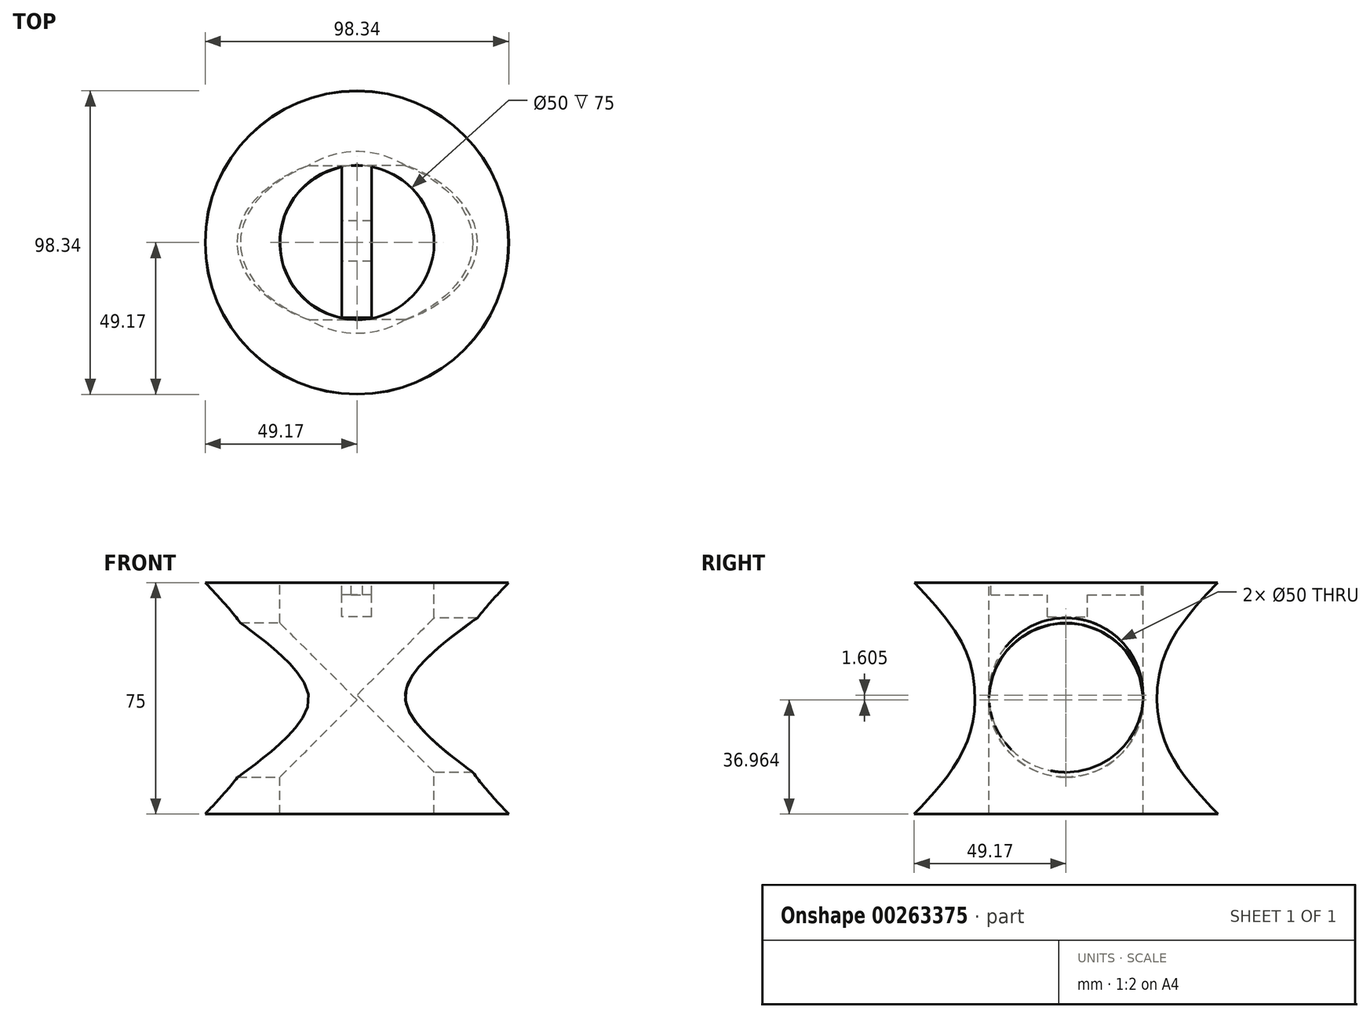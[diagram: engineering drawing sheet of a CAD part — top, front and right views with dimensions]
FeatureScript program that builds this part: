
annotation { "Feature Type Name" : "Feature", "Feature Type Description" : "" }
export const myFeature = defineFeature(function(context is Context, id is Id, definition is map)
    precondition{}
    {
        {
            var Q0;
            Q0=qCreatedBy(makeId("Top.planeOp"),FACE);
            var sketch = newSketch(context, id + "F0", { "sketchPlane" : qUnion([Q0])});
            skCircle(sketch, "E0", {"center": v(0, 0) * mm, "radius": 49.17 * mm});
            skSolve(sketch);
        }
        {
            var Q0;
            Q0=makeQuery(id+"F0.imprint","IMPRINT",FACE,{"disambiguationData":[TD([[makeQuery(id+"F0.imprint","IMPRINT",EDGE,{"derivedFrom":sQuery(id+"F0.wireOp",EDGE,"E0")}),1.0]])]});
            cPlane(context, id + "F1", {"entities" : qUnion([Q0]), "cplaneType" : CPlaneType.OFFSET, "offset" : 25 * mm, "width" : 150 * mm, "height" : 150 * mm});
        }
        {
            var Q0;
            Q0=qCreatedBy(id+"F1.planeOp",FACE);
            var sketch = newSketch(context, id + "F2", { "sketchPlane" : qUnion([Q0])});
            skCircle(sketch, "E1", {"center": v(0, 0) * mm, "radius": 31.5 * mm});
            skSolve(sketch);
        }
        {
            var Q0;
            Q0=qCreatedBy(id+"F1.planeOp",FACE);
            cPlane(context, id + "F3", {"entities" : qUnion([Q0]), "cplaneType" : CPlaneType.OFFSET, "offset" : 25 * mm, "width" : 150 * mm, "height" : 150 * mm});
        }
        {
            var Q0;
            Q0=qCreatedBy(id+"F3.planeOp",FACE);
            var sketch = newSketch(context, id + "F4", { "sketchPlane" : qUnion([Q0])});
            skCircle(sketch, "E2", {"center": v(0, 0) * mm, "radius": 31.39 * mm});
            skSolve(sketch);
        }
        {
            var Q0;
            Q0=qCreatedBy(id+"F3.planeOp",FACE);
            cPlane(context, id + "F5", {"entities" : qUnion([Q0]), "cplaneType" : CPlaneType.OFFSET, "offset" : 25 * mm, "width" : 150 * mm, "height" : 150 * mm});
        }
        {
            var Q0;
            Q0=qCreatedBy(id+"F5.planeOp",FACE);
            var sketch = newSketch(context, id + "F6", { "sketchPlane" : qUnion([Q0])});
            skCircle(sketch, "E3", {"center": v(0, 0) * mm, "radius": 49.12 * mm});
            skSolve(sketch);
        }
        {
            var Q0;
            Q0=makeQuery(id+"F0.imprint","IMPRINT",FACE,{"disambiguationData":[TD([[makeQuery(id+"F0.imprint","IMPRINT",EDGE,{"derivedFrom":sQuery(id+"F0.wireOp",EDGE,"E0")}),1.0]])]});
            var Q1;
            Q1=makeQuery(id+"F2.imprint","IMPRINT",FACE,{"disambiguationData":[TD([[makeQuery(id+"F2.imprint","IMPRINT",EDGE,{"derivedFrom":sQuery(id+"F2.wireOp",EDGE,"E1")}),1.0]])]});
            var Q2;
            Q2=makeQuery(id+"F4.imprint","IMPRINT",FACE,{"disambiguationData":[TD([[makeQuery(id+"F4.imprint","IMPRINT",EDGE,{"derivedFrom":sQuery(id+"F4.wireOp",EDGE,"E2")}),1.0]])]});
            var Q3;
            Q3=makeQuery(id+"F6.imprint","IMPRINT",FACE,{"disambiguationData":[TD([[makeQuery(id+"F6.imprint","IMPRINT",EDGE,{"derivedFrom":sQuery(id+"F6.wireOp",EDGE,"E3")}),1.0]])]});
            loft(context, id + "F7", {"sheetProfilesArray" : [{ "sheetProfileEntities" : qUnion([Q0]) }, { "sheetProfileEntities" : qUnion([Q1]) }, { "sheetProfileEntities" : qUnion([Q2]) }, { "sheetProfileEntities" : qUnion([Q3]) }]});
        }
        {
            var Q0;
            Q0=qCreatedBy(id+"F5.planeOp",FACE);
            var sketch = newSketch(context, id + "F8", { "sketchPlane" : qUnion([Q0])});
            skCircle(sketch, "E4", {"center": v(0, 0) * mm, "radius": 19.4 * mm});
            skSolve(sketch);
        }
        {
            var Q0;
            Q0=qCreatedBy(id+"F1.planeOp",FACE);
            var sketch = newSketch(context, id + "F9", { "sketchPlane" : qUnion([Q0])});
            skCircle(sketch, "E5", {"center": v(0, 0) * mm, "radius": 19.31 * mm});
            skSolve(sketch);
        }
        {
            var Q0;
            Q0=sQuery(id+"F8.wireOp",VERTEX,"E4.center");
            var Q1;
            Q1=sQuery(id+"F9.wireOp",VERTEX,"E5.center");
            var Q2;
            Q2=makeQuery(id+"F7.opLoft","SWEPT_BODY",BODY,{"disambiguationData":[OSD([makeQuery(id+"F0.imprint","IMPRINT",FACE,{"disambiguationData":[TD([[makeQuery(id+"F0.imprint","IMPRINT",EDGE,{"derivedFrom":sQuery(id+"F0.wireOp",EDGE,"E0")}),1.0]])]}),sQuery(id+"F2.wireOp",EDGE,"E1"),sQuery(id+"F4.wireOp",EDGE,"E2"),makeQuery(id+"F6.imprint","IMPRINT",FACE,{"disambiguationData":[TD([[makeQuery(id+"F6.imprint","IMPRINT",EDGE,{"derivedFrom":sQuery(id+"F6.wireOp",EDGE,"E3")}),1.0]])]})])]});
            hole(context, id + "F10", {"style" : HoleStyle.SIMPLE, "endStyle" : HoleEndStyle.BLIND, "holeDiameter" : 50 * mm, "holeDepth" : 75 * mm, "tappedDepth" : 12 * mm, "tapClearance" : 3, "startFromSketch" : true, "locations" : qUnion([Q0, Q1]), "scope" : qUnion([Q2])});
        }
        {
            var Q0;
            Q0=qCreatedBy(makeId("Right.planeOp"),FACE);
            var sketch = newSketch(context, id + "F11", { "sketchPlane" : qUnion([Q0])});
            skCircle(sketch, "E6", {"center": v(0, 38.57) * mm, "radius": 15 * mm});
            skSolve(sketch);
        }
        {
            var Q0;
            Q0=sQuery(id+"F11.wireOp",VERTEX,"E6.center");
            var Q1;
            Q1=makeQuery(id+"F7.opLoft","SWEPT_BODY",BODY,{"disambiguationData":[OSD([makeQuery(id+"F0.imprint","IMPRINT",FACE,{"disambiguationData":[TD([[makeQuery(id+"F0.imprint","IMPRINT",EDGE,{"derivedFrom":sQuery(id+"F0.wireOp",EDGE,"E0")}),1.0]])]}),sQuery(id+"F2.wireOp",EDGE,"E1"),sQuery(id+"F4.wireOp",EDGE,"E2"),makeQuery(id+"F6.imprint","IMPRINT",FACE,{"disambiguationData":[TD([[makeQuery(id+"F6.imprint","IMPRINT",EDGE,{"derivedFrom":sQuery(id+"F6.wireOp",EDGE,"E3")}),1.0]])]})])]});
            hole(context, id + "F12", {"style" : HoleStyle.SIMPLE, "endStyle" : HoleEndStyle.BLIND, "oppositeDirection" : true, "holeDiameter" : 50 * mm, "holeDepth" : 75 * mm, "tappedDepth" : 12 * mm, "tapClearance" : 3, "startFromSketch" : true, "locations" : qUnion([Q0]), "scope" : qUnion([Q1])});
        }
        {
            var Q0;
            Q0=qCreatedBy(makeId("Right.planeOp"),FACE);
            var sketch = newSketch(context, id + "F13", { "sketchPlane" : qUnion([Q0])});
            skCircle(sketch, "E7", {"center": v(0, 36.96) * mm, "radius": 15 * mm});
            skSolve(sketch);
        }
        {
            var Q0;
            Q0=sQuery(id+"F13.wireOp",VERTEX,"E7.center");
            var Q1;
            Q1=makeQuery(id+"F7.opLoft","SWEPT_BODY",BODY,{"disambiguationData":[OSD([makeQuery(id+"F0.imprint","IMPRINT",FACE,{"disambiguationData":[TD([[makeQuery(id+"F0.imprint","IMPRINT",EDGE,{"derivedFrom":sQuery(id+"F0.wireOp",EDGE,"E0")}),1.0]])]}),sQuery(id+"F2.wireOp",EDGE,"E1"),sQuery(id+"F4.wireOp",EDGE,"E2"),makeQuery(id+"F6.imprint","IMPRINT",FACE,{"disambiguationData":[TD([[makeQuery(id+"F6.imprint","IMPRINT",EDGE,{"derivedFrom":sQuery(id+"F6.wireOp",EDGE,"E3")}),1.0]])]})])]});
            hole(context, id + "F14", {"style" : HoleStyle.SIMPLE, "endStyle" : HoleEndStyle.BLIND, "holeDiameter" : 50 * mm, "holeDepth" : 75 * mm, "tappedDepth" : 12 * mm, "tapClearance" : 3, "startFromSketch" : true, "locations" : qUnion([Q0]), "scope" : qUnion([Q1])});
        }
        {
            var Q0;
            Q0=qCreatedBy(id+"F5.planeOp",FACE);
            var sketch = newSketch(context, id + "F15", { "sketchPlane" : qUnion([Q0])});
            skLineSegment(sketch, "E8.bottom", {"start": v(-4.96, -24.35) * mm, "end": v(4.8, -24.35) * mm});
            skLineSegment(sketch, "E8.top", {"start": v(-4.96, 24.93) * mm, "end": v(4.8, 24.93) * mm});
            skLineSegment(sketch, "E8.left", {"start": v(-4.96, -24.35) * mm, "end": v(-4.96, 24.93) * mm});
            skLineSegment(sketch, "E8.right", {"start": v(4.8, -24.35) * mm, "end": v(4.8, 24.93) * mm});
            skSolve(sketch);
        }
        {
            var Q0;
            Q0=makeQuery(id+"F15.imprint","IMPRINT",FACE,{"disambiguationData":[TD([[makeQuery(id+"F15.imprint","IMPRINT",EDGE,{"derivedFrom":sQuery(id+"F15.wireOp",EDGE,"E8.bottom")}),1.0]])]});
            extrude(context, id + "F16", {"entities" : qUnion([Q0]), "operationType" : NewBodyOperationType.ADD, "oppositeDirection" : true, "depth" : 4 * mm});
        }
        {
            var Q0;
            Q0=makeQuery(id+"F16.opExtrude","CAP_FACE",FACE,{"disambiguationData":[OSD([sQuery(id+"F15.wireOp",EDGE,"E8.bottom"),sQuery(id+"F15.wireOp",EDGE,"E8.top"),sQuery(id+"F15.wireOp",EDGE,"E8.left"),sQuery(id+"F15.wireOp",EDGE,"E8.right")])],"isStart":false});
            var sketch = newSketch(context, id + "F17", { "sketchPlane" : qUnion([Q0])});
            skLineSegment(sketch, "E9.bottom", {"start": v(4.8, 6.06) * mm, "end": v(-4.96, 6.06) * mm});
            skLineSegment(sketch, "E9.top", {"start": v(4.8, -7) * mm, "end": v(-4.96, -7) * mm});
            skLineSegment(sketch, "E9.left", {"start": v(4.8, 6.06) * mm, "end": v(4.8, -7) * mm});
            skLineSegment(sketch, "E9.right", {"start": v(-4.96, 6.06) * mm, "end": v(-4.96, -7) * mm});
            skSolve(sketch);
        }
        {
            var Q0;
            Q0=makeQuery(id+"F17.imprint","IMPRINT",FACE,{"disambiguationData":[TD([[makeQuery(id+"F17.imprint","IMPRINT",EDGE,{"derivedFrom":sQuery(id+"F17.wireOp",EDGE,"E9.bottom")}),1.0]])]});
            extrude(context, id + "F18", {"entities" : qUnion([Q0]), "operationType" : NewBodyOperationType.ADD, "depth" : 7.1 * mm});
        }
    });
